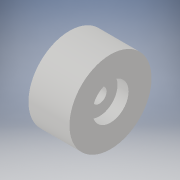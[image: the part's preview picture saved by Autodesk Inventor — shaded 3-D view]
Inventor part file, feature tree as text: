
AUTODESK INVENTOR PART (.ipt)
format: ipt  version: 2018 (Build 220112000, 112)  size: 118,784 bytes
history: native  units: in
note: dims shown in document units (in); Inventor stores cm internally (conversion verified against a paired STEP export)
features: extrude x4, sketch x4
ambient origin geometry x8: Origin, YZ Plane, XZ Plane, XY Plane, X Axis, Y Axis, Z Axis, Center Point
bodies: Solid1 (feature_tree)
feature tree (8):
  extrude  "Extrusion1"  Depth=1.0in TaperAngle=0.0deg
  extrude  "Extrusion2"  Depth=0.27in TaperAngle=0.0deg
  extrude  "Extrusion3"  Depth=0.27in TaperAngle=0.0deg
  extrude  "Extrusion8"  Depth=0.3937in TaperAngle=0.0deg
  sketch  "Sketch1"  dims[d3=0.35in d4=1.0in d5=0.0in]
  sketch  "Sketch2"  dims[d6=0.865in d7=0.27in d8=0.0in]
  sketch  "Sketch3"  dims[d9=0.865in d10=0.27in d11=0.0in]
  sketch  "Sketch5"  dims[d48=0.88in d49=0.3937in d50=0.0in]
